# Revit family: Kulture Capaldi
name_source: partatom
category: Furniture
units: mm (PartAtom-declared; Revit-internal decimal feet)

## family parameters
Always vertical = Yes
Cut with Voids When Loaded = No
OmniClass Number = 23.40.00.00
OmniClass Title = Equipment and Furnishings
Room Calculation Point = No
Shared = No
Work Plane-Based = No

## types (5) — shared parameters
Assembly Code = E2020200
Frame = Gresham - BLACK METAL
Manufacturer = Gresham Office Funiture
Model = KULTURE CAPALDI
Range = SEATING
Seat = Gresham - Camira  Trail - HTL05
URL = www.gof.co.uk

## per-type parameters (varying)
| type | Depth | Height | Product Code | Width |
| Seating - 1180 x 295 x 762 | 295 mm  [stored 0.967848 ft] | 762 mm  [stored 2.5 ft] | KCBACK | 1180 mm  [stored 3.87139 ft] |
| Seating - 1180 x 590 x 440 | 590 mm  [stored 1.9357 ft] | 440 mm  [stored 1.44357 ft] | KCSEAT | 1180 mm  [stored 3.87139 ft] |
| Seating - 590 x 295 x 630 | 295 mm  [stored 0.967848 ft] | 630 mm  [stored 2.06693 ft] | KCSARM | 590 mm  [stored 1.9357 ft] |
| Seating - 885 x 295 x 630 | 295 mm  [stored 0.967848 ft] | 630 mm  [stored 2.06693 ft] | KCLARM | 885 mm |
| Seating - 1475 x 590 x 440 | 590 mm  [stored 1.9357 ft] | 440 mm  [stored 1.44357 ft] | KCSEATING | 1475 mm  [stored 4.83924 ft] |

note: [stored X ft] marks values corroborated as IEEE doubles in the binary element streams (Revit-internal decimal feet)

## geometry (parser evidence)
native form markers: Sweep x2
no freeform markers — native parametric forms only
